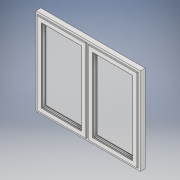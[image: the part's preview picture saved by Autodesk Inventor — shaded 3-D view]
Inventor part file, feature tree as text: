
AUTODESK INVENTOR PART (.ipt)
format: ipt  version: 2019 (Build 230136000, 136)  size: 263,680 bytes
history: native  units: mm
features: other x6, sketch x3, pattern_linear x3, sweep x2, extrude x1, projected_geometry x1
ambient origin geometry x8: Origin, YZ Plane, XZ Plane, XY Plane, X Axis, Y Axis, Z Axis, Center Point
bodies: Body1 (feature_tree), Body2 (feature_tree), Body3 (feature_tree)
feature tree (16):
  other  "Таблица"
  other  "Окно 2 рамы-01"
  other  "Окно 2 рамы-02"
  other  "Обвязка"
  sketch  "Эскиз1"
  sketch  "Эскиз2"
  sweep  "Сдвиг1"
  pattern_linear  "Прямоуг.массив1"  Spacing1=0.0mm  [1 undecoded]
  sweep  "Сдвиг2"
  extrude  "Выдавливание1"  TaperAngle=0.0deg  [1 undecoded]
  pattern_linear  "Прямоуг.массив2"  Spacing1=10.0mm  [1 undecoded]
  pattern_linear  "Прямоуг.массив3"  Count1=3 Spacing1=21.5mm
  other  "Рама"
  sketch  "Эскиз3"
  projected_geometry  "Спроецированная петля1"
  other  "Стекло"
note: 3 required parameter values undecoded (feature->parameter linkage not recoverable at this tier; creation-order binding heuristic only, values carry confidence <= 0.55)
